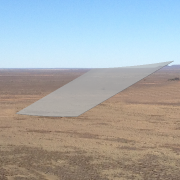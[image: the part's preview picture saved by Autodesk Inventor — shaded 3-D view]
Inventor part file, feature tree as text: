
AUTODESK INVENTOR PART (.ipt)
format: ipt  version: 2013 SP2 (Build 170200200, 200)  size: 150,016 bytes
history: native  units: in
note: dims shown in document units (in); Inventor stores cm internally (conversion verified against a paired STEP export)
features: sketch x3, sweep x1, extrude x1, other x1
ambient origin geometry x8: Origin, YZ Plane, XZ Plane, XY Plane, X Axis, Y Axis, Z Axis, Center Point
feature tree (6):
  sweep  "Sweep2"
  extrude  "Extrusion3"  TaperAngle=0.0deg  [1 undecoded]
  sketch  "Sketch3"  dims[d6=0.0in d7=277.0in d8=90.0in]
  other  "2D Equation Curve2"
  sketch  "Sketch4"  dims[d10=0.25in d11=0.0in]
  sketch  "Sketch8"  dims[d28=2.0in d29=2.0in d32=2.0in d33=300.0in d34=1.1853in d35=163.0in d36=206.0in d37=300.0in d38=0.0in]
note: 1 required parameter value undecoded (feature->parameter linkage not recoverable at this tier; creation-order binding heuristic only, values carry confidence <= 0.55)
